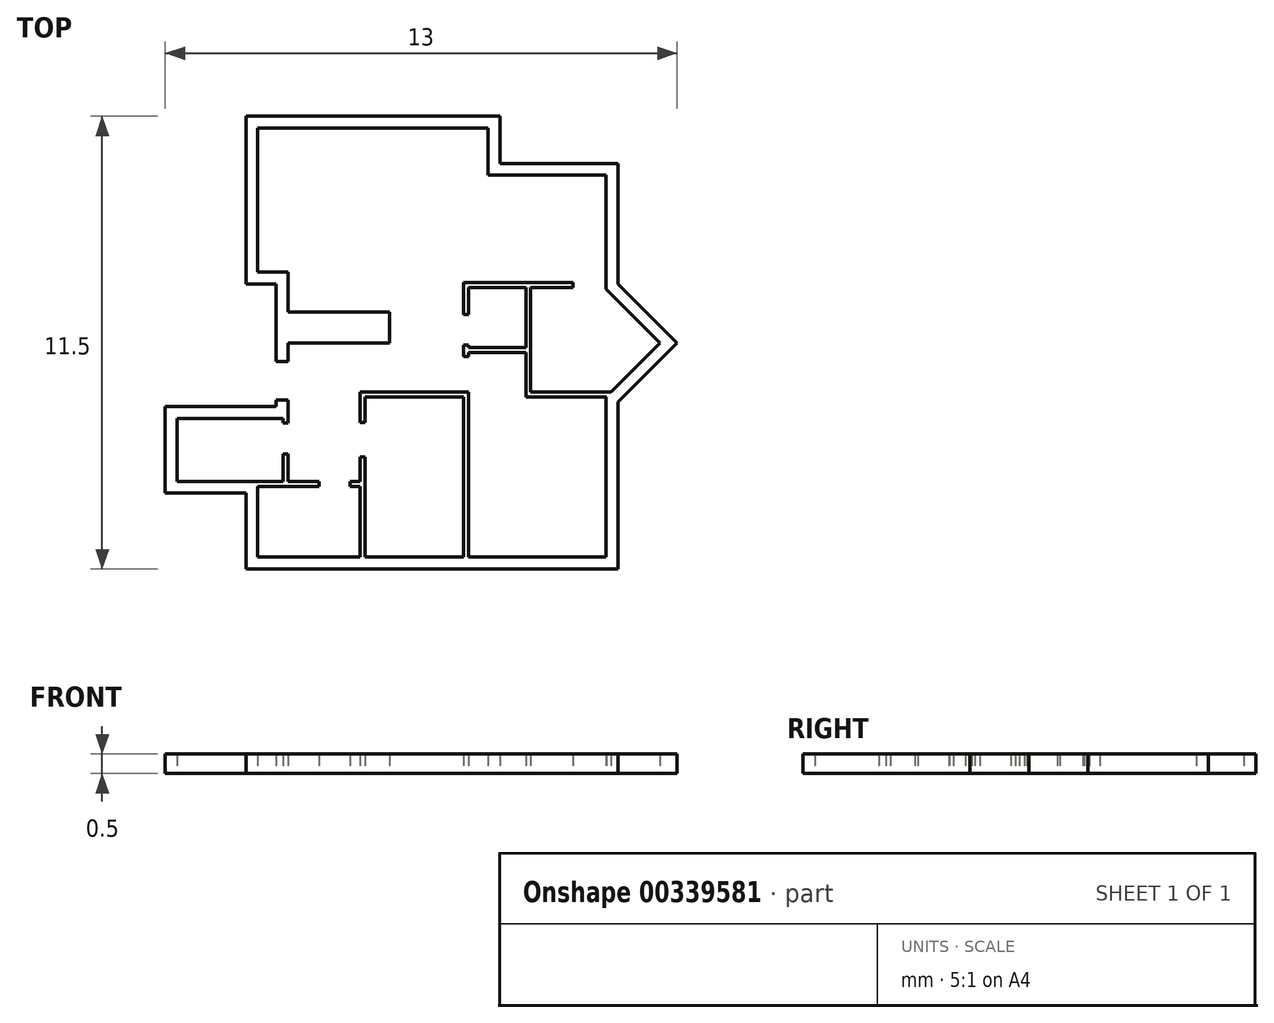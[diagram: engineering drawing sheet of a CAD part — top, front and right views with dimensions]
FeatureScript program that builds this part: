
annotation { "Feature Type Name" : "Feature", "Feature Type Description" : "" }
export const myFeature = defineFeature(function(context is Context, id is Id, definition is map)
    precondition{}
    {
        {
            var Q0;
            Q0=qCreatedBy(makeId("Top.planeOp"),FACE);
            var sketch = newSketch(context, id + "F0", { "sketchPlane" : qUnion([Q0])});
            skLineSegment(sketch, "E0", {"start": v(4.1, -5.7) * mm, "end": v(-5.34, -5.7) * mm});
            skLineSegment(sketch, "E1", {"start": v(-5.34, -5.7) * mm, "end": v(-5.34, -3.77) * mm});
            skLineSegment(sketch, "E2", {"start": v(-5.34, -3.77) * mm, "end": v(-7.4, -3.77) * mm});
            skLineSegment(sketch, "E3", {"start": v(-7.4, -3.77) * mm, "end": v(-7.4, -1.57) * mm});
            skLineSegment(sketch, "E4", {"start": v(-7.4, -1.57) * mm, "end": v(-4.57, -1.57) * mm});
            skLineSegment(sketch, "E5", {"start": v(-4.57, -1.57) * mm, "end": v(-4.57, -1.4) * mm});
            skLineSegment(sketch, "E6", {"start": v(-4.57, 1.54) * mm, "end": v(-5.34, 1.54) * mm});
            skLineSegment(sketch, "E7", {"start": v(-5.34, 1.54) * mm, "end": v(-5.34, 5.8) * mm});
            skLineSegment(sketch, "E8", {"start": v(-5.34, 5.8) * mm, "end": v(1.1, 5.8) * mm});
            skLineSegment(sketch, "E9", {"start": v(1.1, 5.8) * mm, "end": v(1.1, 4.6) * mm});
            skLineSegment(sketch, "E10", {"start": v(1.1, 4.6) * mm, "end": v(4.1, 4.6) * mm});
            skLineSegment(sketch, "E11", {"start": v(4.1, 4.6) * mm, "end": v(4.1, 1.54) * mm});
            skLineSegment(sketch, "E12", {"start": v(4.1, 1.54) * mm, "end": v(5.6, 0.04) * mm});
            skLineSegment(sketch, "E13", {"start": v(5.6, 0.04) * mm, "end": v(4.1, -1.46) * mm});
            skLineSegment(sketch, "E14", {"start": v(4.1, -1.46) * mm, "end": v(4.1, -5.7) * mm});
            skLineSegment(sketch, "E15.0", {"start": v(-5.04, 1.84) * mm, "end": v(-5.04, 5.5) * mm});
            skLineSegment(sketch, "E15.1", {"start": v(-4.27, 1.84) * mm, "end": v(-5.04, 1.84) * mm});
            skLineSegment(sketch, "E15.2", {"start": v(-4.27, -2) * mm, "end": v(-4.27, -1.4) * mm});
            skLineSegment(sketch, "E15.3", {"start": v(-7.1, -1.87) * mm, "end": v(-4.4, -1.87) * mm});
            skLineSegment(sketch, "E15.4", {"start": v(3.8, 1.42) * mm, "end": v(5.18, 0.04) * mm});
            skLineSegment(sketch, "E15.5", {"start": v(3.8, 4.3) * mm, "end": v(3.8, 1.42) * mm});
            skLineSegment(sketch, "E15.6", {"start": v(0.8, 4.3) * mm, "end": v(3.8, 4.3) * mm});
            skLineSegment(sketch, "E15.7", {"start": v(0.8, 5.5) * mm, "end": v(0.8, 4.3) * mm});
            skLineSegment(sketch, "E15.8", {"start": v(5.18, 0.04) * mm, "end": v(3.94, -1.2) * mm});
            skLineSegment(sketch, "E15.9", {"start": v(3.8, -1.33) * mm, "end": v(3.8, -5.4) * mm});
            skLineSegment(sketch, "E15.10", {"start": v(3.8, -5.4) * mm, "end": v(0.3, -5.4) * mm});
            skLineSegment(sketch, "E15.11", {"start": v(-5.04, -5.4) * mm, "end": v(-5.04, -3.6) * mm});
            skLineSegment(sketch, "E15.12", {"start": v(-5.04, 5.5) * mm, "end": v(0.8, 5.5) * mm});
            skLineSegment(sketch, "E15.13", {"start": v(-3.48, -3.47) * mm, "end": v(-4.27, -3.47) * mm});
            skLineSegment(sketch, "E15.14", {"start": v(-7.1, -3.47) * mm, "end": v(-7.1, -1.87) * mm});
            skLineSegment(sketch, "E16", {"start": v(-3.48, -3.47) * mm, "end": v(-3.48, -3.6) * mm});
            skLineSegment(sketch, "E17", {"start": v(-3.48, -3.6) * mm, "end": v(-5.04, -3.6) * mm});
            skPoint(sketch, "E18.orphan", {"position": v(-5.04, -3.47) * mm});
            skLineSegment(sketch, "E19", {"start": v(-4.4, -3.47) * mm, "end": v(-4.4, -2.77) * mm});
            skLineSegment(sketch, "E20", {"start": v(-4.4, -2.77) * mm, "end": v(-4.27, -2.77) * mm});
            skLineSegment(sketch, "E21", {"start": v(-4.27, -2.77) * mm, "end": v(-4.27, -3.47) * mm});
            skLineSegment(sketch, "E22.trimOffspring", {"start": v(-4.4, -3.47) * mm, "end": v(-7.1, -3.47) * mm});
            skLineSegment(sketch, "E23", {"start": v(-4.4, -1.87) * mm, "end": v(-4.4, -2) * mm});
            skLineSegment(sketch, "E24", {"start": v(-4.4, -2) * mm, "end": v(-4.27, -2) * mm});
            skLineSegment(sketch, "E25", {"start": v(-4.57, -1.4) * mm, "end": v(-4.27, -1.4) * mm});
            skLineSegment(sketch, "E26", {"start": v(-4.57, -0.42) * mm, "end": v(-4.27, -0.42) * mm});
            skLineSegment(sketch, "E27.trimOffspring", {"start": v(-4.27, -0.42) * mm, "end": v(-4.27, 1.84) * mm});
            skLineSegment(sketch, "E28.trimOffspring", {"start": v(-4.57, -0.42) * mm, "end": v(-4.57, 1.54) * mm});
            skLineSegment(sketch, "E29", {"start": v(-4.27, 0.82) * mm, "end": v(-1.7, 0.82) * mm});
            skLineSegment(sketch, "E30", {"start": v(-1.7, 0.82) * mm, "end": v(-1.7, 0.04) * mm});
            skLineSegment(sketch, "E31", {"start": v(-1.7, 0.04) * mm, "end": v(-4.27, 0.04) * mm});
            skLineSegment(sketch, "E32", {"start": v(0.18, 0.77) * mm, "end": v(0.18, 1.57) * mm});
            skLineSegment(sketch, "E33", {"start": v(0.18, 1.57) * mm, "end": v(2.97, 1.57) * mm});
            skLineSegment(sketch, "E34", {"start": v(2.97, 1.57) * mm, "end": v(2.97, 1.45) * mm});
            skLineSegment(sketch, "E35", {"start": v(2.97, 1.45) * mm, "end": v(1.9, 1.45) * mm});
            skLineSegment(sketch, "E36", {"start": v(1.9, 1.45) * mm, "end": v(1.9, -1.2) * mm});
            skLineSegment(sketch, "E37", {"start": v(1.9, -1.2) * mm, "end": v(3.94, -1.2) * mm});
            skLineSegment(sketch, "E38", {"start": v(1.77, -1.33) * mm, "end": v(1.77, -0.2) * mm});
            skLineSegment(sketch, "E39", {"start": v(1.77, -0.2) * mm, "end": v(0.3, -0.2) * mm});
            skLineSegment(sketch, "E40", {"start": v(0.3, -0.08) * mm, "end": v(1.77, -0.08) * mm});
            skLineSegment(sketch, "E41", {"start": v(1.77, -0.08) * mm, "end": v(1.77, 1.45) * mm});
            skLineSegment(sketch, "E42", {"start": v(1.77, 1.45) * mm, "end": v(0.3, 1.45) * mm});
            skLineSegment(sketch, "E43", {"start": v(0.3, 1.45) * mm, "end": v(0.3, 0.77) * mm});
            skLineSegment(sketch, "E44", {"start": v(0.3, 0.77) * mm, "end": v(0.18, 0.77) * mm});
            skLineSegment(sketch, "E45", {"start": v(0.3, -0.08) * mm, "end": v(0.3, -0.01) * mm});
            skLineSegment(sketch, "E46", {"start": v(0.3, -0.01) * mm, "end": v(0.18, -0.01) * mm});
            skLineSegment(sketch, "E47", {"start": v(0.18, -0.01) * mm, "end": v(0.18, -0.3) * mm});
            skLineSegment(sketch, "E48", {"start": v(0.18, -0.3) * mm, "end": v(0.3, -0.3) * mm});
            skLineSegment(sketch, "E49", {"start": v(0.3, -0.3) * mm, "end": v(0.3, -0.2) * mm});
            skLineSegment(sketch, "E50.trimOffspring", {"start": v(3.8, -1.33) * mm, "end": v(1.77, -1.33) * mm});
            skLineSegment(sketch, "E51", {"start": v(-2.44, -5.4) * mm, "end": v(-2.44, -3.6) * mm});
            skLineSegment(sketch, "E52", {"start": v(-2.44, -3.6) * mm, "end": v(-2.7, -3.6) * mm});
            skLineSegment(sketch, "E53", {"start": v(-2.7, -3.6) * mm, "end": v(-2.7, -3.47) * mm});
            skLineSegment(sketch, "E54", {"start": v(-2.7, -3.47) * mm, "end": v(-2.44, -3.47) * mm});
            skLineSegment(sketch, "E55", {"start": v(-2.44, -3.47) * mm, "end": v(-2.44, -2.86) * mm});
            skLineSegment(sketch, "E56", {"start": v(-2.44, -2.86) * mm, "end": v(-2.32, -2.86) * mm});
            skLineSegment(sketch, "E57", {"start": v(-2.32, -2.86) * mm, "end": v(-2.32, -5.4) * mm});
            skLineSegment(sketch, "E58", {"start": v(-2.44, -1.98) * mm, "end": v(-2.44, -1.2) * mm});
            skLineSegment(sketch, "E59", {"start": v(-2.44, -1.2) * mm, "end": v(0.18, -1.2) * mm});
            skLineSegment(sketch, "E60", {"start": v(0.3, -1.2) * mm, "end": v(0.3, -5.4) * mm});
            skLineSegment(sketch, "E61", {"start": v(-2.44, -1.98) * mm, "end": v(-2.32, -1.98) * mm});
            skLineSegment(sketch, "E62", {"start": v(-2.32, -1.98) * mm, "end": v(-2.32, -1.33) * mm});
            skLineSegment(sketch, "E63", {"start": v(-2.32, -1.33) * mm, "end": v(0.18, -1.33) * mm});
            skLineSegment(sketch, "E64", {"start": v(0.18, -1.33) * mm, "end": v(0.18, -5.4) * mm});
            skLineSegment(sketch, "E65.trimOffspring", {"start": v(-2.44, -5.4) * mm, "end": v(-5.04, -5.4) * mm});
            skLineSegment(sketch, "E66.trimOffspring", {"start": v(0.18, -5.4) * mm, "end": v(-2.32, -5.4) * mm});
            skLineSegment(sketch, "E67", {"start": v(0.18, -1.2) * mm, "end": v(0.18, -1.2) * mm});
            skLineSegment(sketch, "E68", {"start": v(0.18, -1.2) * mm, "end": v(0.3, -1.2) * mm});
            skPoint(sketch, "E69.orphan", {"position": v(0.3, -1.2) * mm});
            skLineSegment(sketch, "E70", {"start": v(3.8, -1.33) * mm, "end": v(3.81, -1.33) * mm});
            skLineSegment(sketch, "E71.trimOffspring", {"start": v(3.81, -1.33) * mm, "end": v(3.8, -1.33) * mm});
            skSolve(sketch);
        }
        {
            var Q0;
            Q0 = qSketchRegion(id + "F0", true);
            extrude(context, id + "F1", {"entities" : qUnion([Q0]), "depth" : 0.5 * mm});
        }
    });
